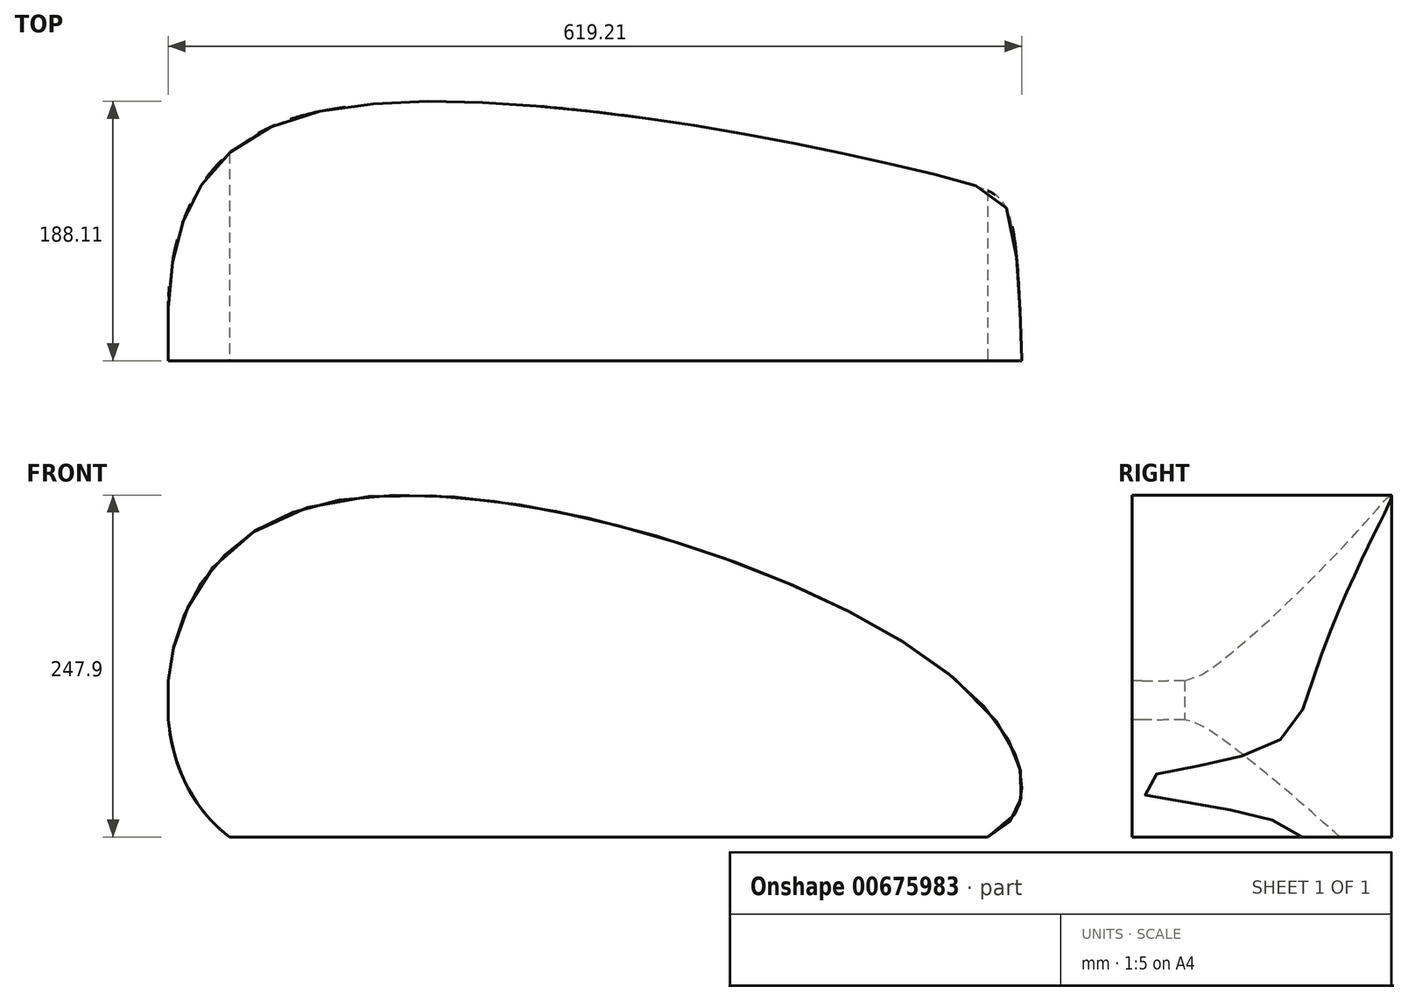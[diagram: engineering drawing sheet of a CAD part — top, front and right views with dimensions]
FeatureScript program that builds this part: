
annotation { "Feature Type Name" : "Feature", "Feature Type Description" : "" }
export const myFeature = defineFeature(function(context is Context, id is Id, definition is map)
    precondition{}
    {
        {
            var Q0;
            Q0=qCreatedBy(makeId("Front.planeOp"),FACE);
            var sketch = newSketch(context, id + "F0", { "sketchPlane" : qUnion([Q0])});
            skLineSegment(sketch, "E0", {"start": v(58.06, 0) * mm, "end": v(608.06, 0) * mm});
            skFitSpline(sketch, "E1", {"points": [v(58.06, 0) * mm, v(13.73, 113.17) * mm, v(125.85, 241.94) * mm, v(608.06, 91.77) * mm, v(608.06, 0) * mm], "startDerivative": vector(-516.49, 398.55) * mm, "endDerivative": vector(-573.7, -240.26) * mm});
            skLineSegment(sketch, "E2", {"start": v(13.73, 113.17) * mm, "end": v(13.73, 84.98) * mm});
            skPoint(sketch, "E3.end.orphan", {"position": v(13.73, 0) * mm});
            skPoint(sketch, "E3.start.orphan", {"position": v(0, 0) * mm});
            skPoint(sketch, "E4.trimOffspring.end.orphan", {"position": v(650, 0) * mm});
            skPoint(sketch, "E5.end.orphan", {"position": v(632.94, 0) * mm});
            skSolve(sketch);
        }
        {
            var Q0;
            Q0=qCreatedBy(makeId("Top.planeOp"),FACE);
            var sketch = newSketch(context, id + "F1", { "sketchPlane" : qUnion([Q0])});
            skLineSegment(sketch, "E6.bottom", {"start": v(13.73, 0) * mm, "end": v(632.94, 0) * mm, "construction": true});
            skLineSegment(sketch, "E7", {"start": v(13.73, 0) * mm, "end": v(632.94, 0) * mm});
            skFitSpline(sketch, "E8", {"points": [v(13.73, 0) * mm, v(13.73, 25) * mm, v(17.73, 76.56) * mm, v(104.02, 174.74) * mm, v(582.67, 131.23) * mm, v(624.76, 100.13) * mm, v(632.94, 0) * mm], "startDerivative": vector(0, 266.13) * mm, "endDerivative": vector(-15.7, -736.51) * mm});
            skPoint(sketch, "E9.orphan", {"position": v(650, 0) * mm});
            skPoint(sketch, "E10.orphan", {"position": v(0, 0) * mm});
            skPoint(sketch, "E11.orphan", {"position": v(13.73, 50) * mm});
            skSolve(sketch);
        }
        {
            var Q0;
            Q0=makeQuery(id+"F1.imprint","IMPRINT",FACE,{"disambiguationData":[TD([[makeQuery(id+"F1.imprint","IMPRINT",EDGE,{"derivedFrom":sQuery(id+"F1.wireOp",EDGE,"E7")}),1.0]])]});
            var sketch = newSketch(context, id + "F2", { "sketchPlane" : qUnion([Q0])});
            skLineSegment(sketch, "E12", {"start": v(633.01, 0) * mm, "end": v(13.73, 0) * mm});
            skFitSpline(sketch, "E13", {"points": [v(13.73, 0) * mm, v(13.73, 25.6) * mm, v(17.64, 76.62) * mm, v(104.95, 176.03) * mm, v(584.1, 131.32) * mm, v(625.12, 100.82) * mm, v(633.01, 0) * mm], "startDerivative": vector(-0.75, 299.5) * mm, "endDerivative": vector(26.44, -313.59) * mm});
            skSolve(sketch);
        }
        {
            var Q0;
            {var subQ0=sQuery(id+"F0.wireOp",EDGE,"E0");Q0=makeQuery(id+"F0.imprint","IMPRINT",FACE,{"disambiguationData":[TD([[makeQuery(id+"F0.imprint","IMPRINT",EDGE,{"derivedFrom":subQ0}),1.0]])]});}
            extrude(context, id + "F3", {"entities" : qUnion([Q0]), "oppositeDirection" : true, "depth" : 250 * mm, "offsetDistance" : 25 * mm});
        }
        {
            var Q0;
            Q0 = qSketchRegion(id + "F2", true);
            extrude(context, id + "F4", {"entities" : qUnion([Q0]), "operationType" : NewBodyOperationType.INTERSECT, "depth" : 250 * mm, "offsetDistance" : 25 * mm});
        }
    });
